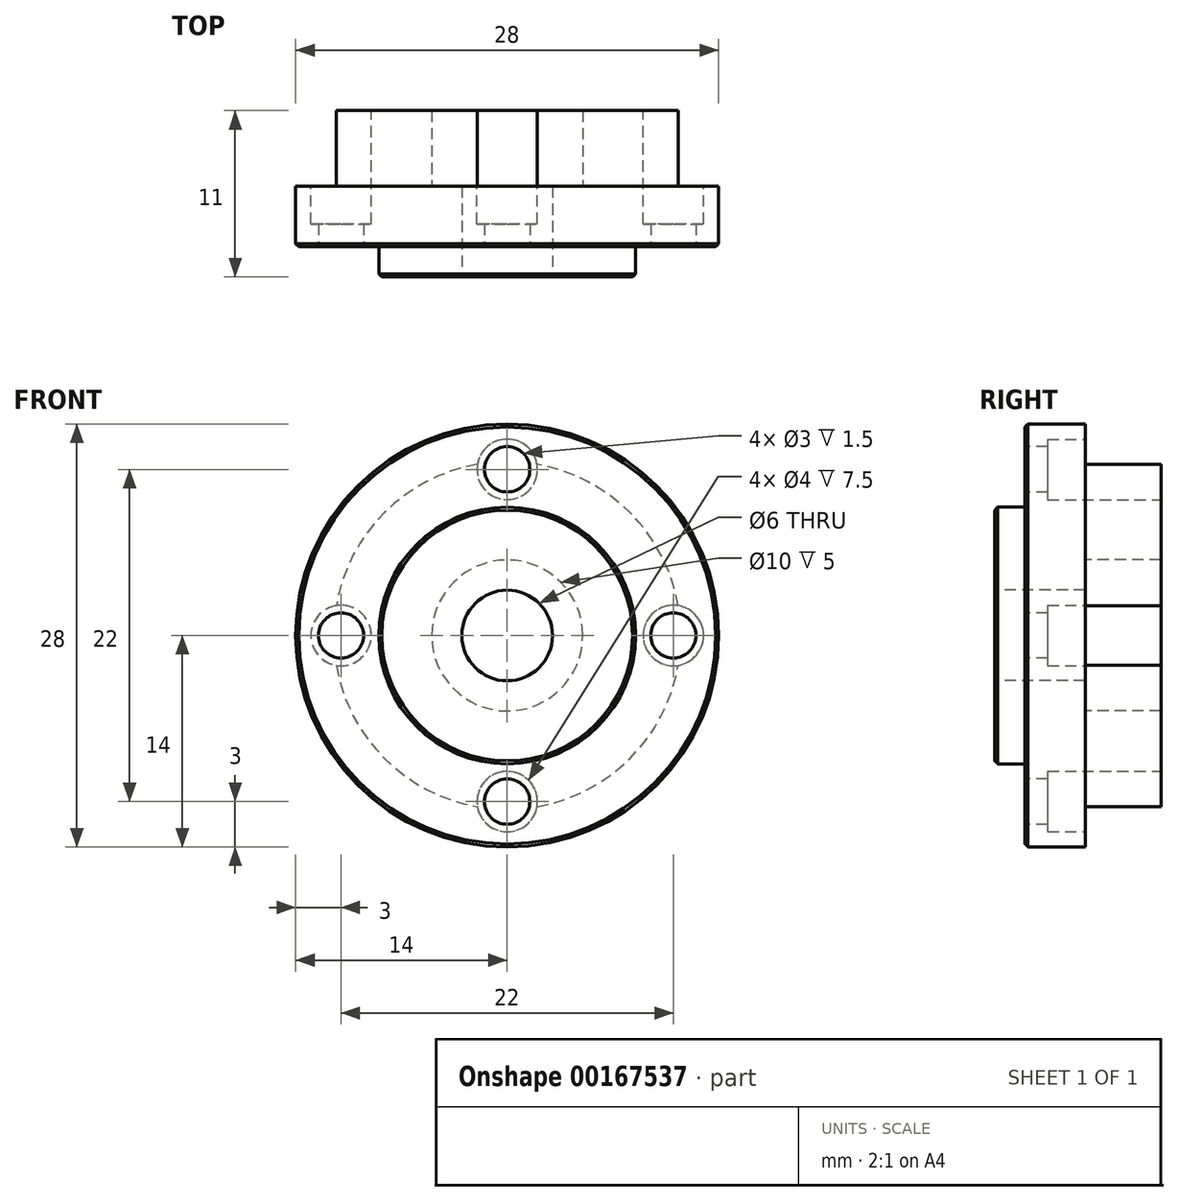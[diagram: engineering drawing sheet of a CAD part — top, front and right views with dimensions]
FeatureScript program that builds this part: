
annotation { "Feature Type Name" : "Feature", "Feature Type Description" : "" }
export const myFeature = defineFeature(function(context is Context, id is Id, definition is map)
    precondition{}
    {
        {
            var Q0;
            Q0=qCreatedBy(makeId("Front.planeOp"),FACE);
            var sketch = newSketch(context, id + "F0", { "sketchPlane" : qUnion([Q0])});
            skCircle(sketch, "E0", {"center": v(0, 0) * mm, "radius": 14 * mm});
            skLineSegment(sketch, "E1", {"start": v(0, 21.9) * mm, "end": v(0, -21.86) * mm, "construction": true});
            skLineSegment(sketch, "E2", {"start": v(-20.2, 0) * mm, "end": v(21.4, 0) * mm, "construction": true});
            skCircle(sketch, "E3", {"center": v(0, 0) * mm, "radius": 11 * mm, "construction": true});
            skCircle(sketch, "E4", {"center": v(0, 11) * mm, "radius": 1.5 * mm});
            skCircle(sketch, "E5.1.0", {"center": v(-11, 0) * mm, "radius": 1.5 * mm});
            skCircle(sketch, "E5.2.0", {"center": v(0, -11) * mm, "radius": 1.5 * mm});
            skCircle(sketch, "E5.3.0", {"center": v(11, 0) * mm, "radius": 1.5 * mm});
            skCircle(sketch, "E6", {"center": v(0, 0) * mm, "radius": 3 * mm});
            skSolve(sketch);
        }
        {
            var Q0;
            Q0=qSketchRegion(id+"F0",true);
            extrude(context, id + "F1", {"entities" : qUnion([Q0]), "oppositeDirection" : true, "depth" : 4 * mm});
        }
        {
            var Q0;
            Q0=qCreatedBy(makeId("Front.planeOp"),FACE);
            var sketch = newSketch(context, id + "F2", { "sketchPlane" : qUnion([Q0])});
            skCircle(sketch, "E7", {"center": v(0, 0) * mm, "radius": 8.5 * mm});
            skCircle(sketch, "E8.0", {"center": v(0, 0) * mm, "radius": 3 * mm});
            skSolve(sketch);
        }
        {
            var Q0;
            Q0=qSketchRegion(id+"F2",true);
            extrude(context, id + "F3", {"entities" : qUnion([Q0]), "operationType" : NewBodyOperationType.ADD, "depth" : 2 * mm});
        }
        {
            var Q0;
            Q0=makeQuery(id+"F3.opExtrude","CAP_EDGE",EDGE,{"disambiguationData":[OSD([sQuery(id+"F2.wireOp",EDGE,"E7")])],"isStart":false});
            var Q1;
            Q1=makeQuery(id+"F1.opExtrude","CAP_EDGE",EDGE,{"disambiguationData":[OSD([sQuery(id+"F0.wireOp",EDGE,"E0")])],"isStart":true});
            chamfer(context, id + "F4", {"entities" : qUnion([Q0, Q1]), "width" : 0.2 * mm, "tangentPropagation" : true});
        }
        {
            var Q0;
            Q0=makeQuery(id+"F1.opExtrude","CAP_FACE",FACE,{"disambiguationData":[OSD([sQuery(id+"F0.wireOp",EDGE,"E0"),sQuery(id+"F0.wireOp",EDGE,"E4"),sQuery(id+"F0.wireOp",EDGE,"E5.1.0"),sQuery(id+"F0.wireOp",EDGE,"E5.2.0"),sQuery(id+"F0.wireOp",EDGE,"E5.3.0"),sQuery(id+"F0.wireOp",EDGE,"E6")])],"isStart":false});
            var sketch = newSketch(context, id + "F5", { "sketchPlane" : qUnion([Q0])});
            skCircle(sketch, "E9", {"center": v(0, 0) * mm, "radius": 5 * mm});
            skCircle(sketch, "E10", {"center": v(0, 0) * mm, "radius": 11.5 * mm});
            skSolve(sketch);
        }
        {
            var Q0;
            Q0=qSketchRegion(id+"F5",true);
            extrude(context, id + "F6", {"entities" : qUnion([Q0]), "operationType" : NewBodyOperationType.ADD, "depth" : 5 * mm});
        }
        {
            var Q0;
            Q0=makeQuery(id+"F6.opExtrude","CAP_FACE",FACE,{"disambiguationData":[OSD([sQuery(id+"F5.wireOp",EDGE,"E9"),sQuery(id+"F5.wireOp",EDGE,"E10")])],"isStart":false});
            var sketch = newSketch(context, id + "F7", { "sketchPlane" : qUnion([Q0])});
            skCircle(sketch, "E11.0", {"center": v(-11, 0) * mm, "radius": 1.5 * mm, "construction": true});
            skCircle(sketch, "E12.0", {"center": v(-11, 0) * mm, "radius": 2 * mm});
            skCircle(sketch, "E13.1.0", {"center": v(0, -11) * mm, "radius": 2 * mm});
            skCircle(sketch, "E13.2.0", {"center": v(11, 0) * mm, "radius": 2 * mm});
            skCircle(sketch, "E13.3.0", {"center": v(0, 11) * mm, "radius": 2 * mm});
            skPoint(sketch, "E13.center", {"position": v(0, 0) * mm});
            skSolve(sketch);
        }
        {
            var Q0;
            Q0=qSketchRegion(id+"F7",true);
            extrude(context, id + "F8", {"entities" : qUnion([Q0]), "operationType" : NewBodyOperationType.REMOVE, "oppositeDirection" : true, "depth" : 7.5 * mm});
        }
    });
